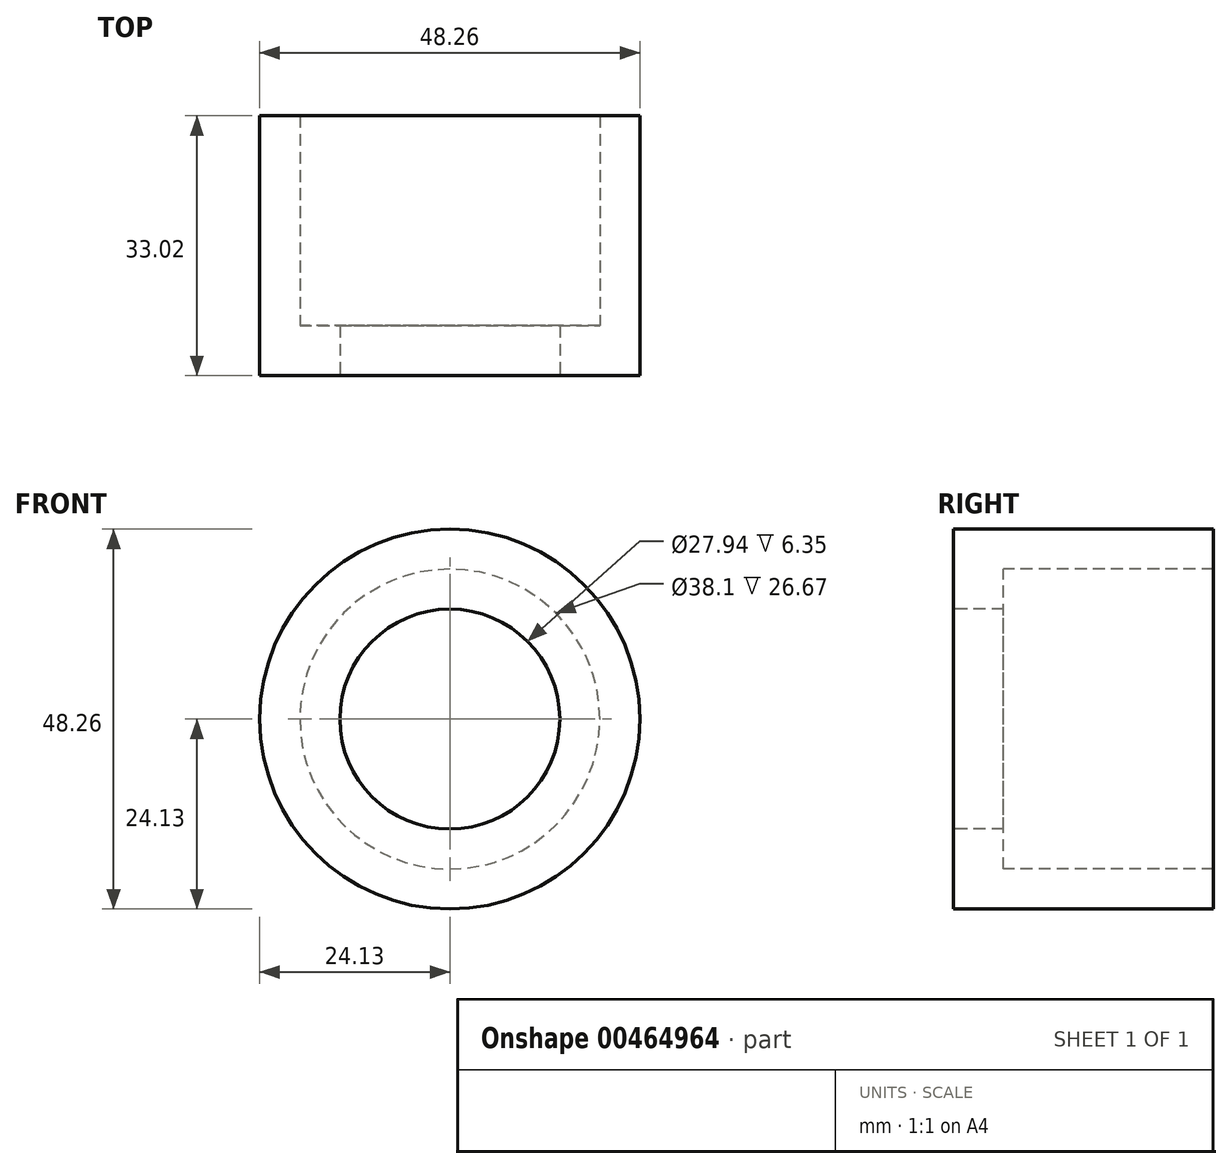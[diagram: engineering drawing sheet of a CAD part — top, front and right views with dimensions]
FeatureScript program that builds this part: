
annotation { "Feature Type Name" : "Feature", "Feature Type Description" : "" }
export const myFeature = defineFeature(function(context is Context, id is Id, definition is map)
    precondition{}
    {
        {
            var Q0;
            Q0=qCreatedBy(makeId("Top.planeOp"),FACE);
            var sketch = newSketch(context, id + "F0", { "sketchPlane" : qUnion([Q0])});
            skLineSegment(sketch, "E0", {"start": v(13.97, 0) * mm, "end": v(24.13, 0) * mm});
            skLineSegment(sketch, "E1", {"start": v(24.13, 0) * mm, "end": v(24.13, 33.02) * mm});
            skLineSegment(sketch, "E2", {"start": v(24.13, 33.02) * mm, "end": v(19.05, 33.02) * mm});
            skLineSegment(sketch, "E3", {"start": v(19.05, 33.02) * mm, "end": v(19.05, 6.35) * mm});
            skLineSegment(sketch, "E4", {"start": v(19.05, 6.35) * mm, "end": v(13.97, 6.35) * mm});
            skLineSegment(sketch, "E5", {"start": v(13.97, 6.35) * mm, "end": v(13.97, 0) * mm});
            skLineSegment(sketch, "E6", {"start": v(0, 0) * mm, "end": v(0, 248.77) * mm, "construction": true});
            skSolve(sketch);
        }
        {
            var Q0;
            Q0=makeQuery(id+"F0.imprint","IMPRINT",FACE,{"disambiguationData":[TD([[makeQuery(id+"F0.imprint","IMPRINT",EDGE,{"derivedFrom":sQuery(id+"F0.wireOp",EDGE,"E0")}),1.0]])]});
            var Q1;
            Q1=sQuery(id+"F0.wireOp",EDGE,"E6");
            revolve(context, id + "F1", {"entities" : qUnion([Q0]), "axis" : qUnion([Q1]), "revolveType" : RevolveType.FULL});
        }
    });
